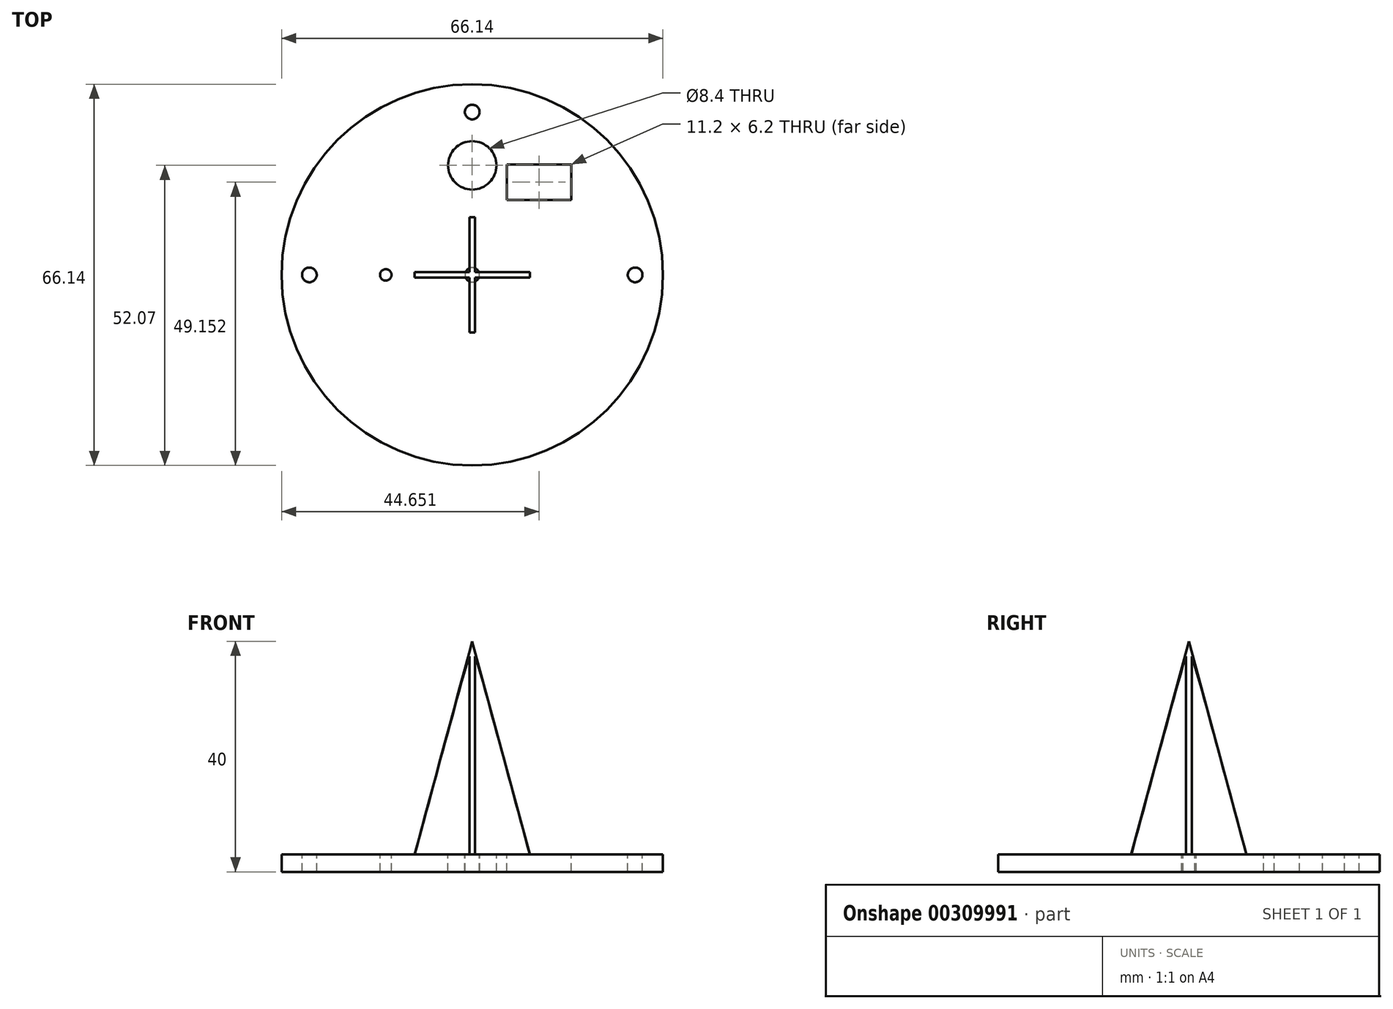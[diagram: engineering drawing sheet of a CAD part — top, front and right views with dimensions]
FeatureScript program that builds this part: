
annotation { "Feature Type Name" : "Feature", "Feature Type Description" : "" }
export const myFeature = defineFeature(function(context is Context, id is Id, definition is map)
    precondition{}
    {
        {
            var Q0;
            Q0=qCreatedBy(makeId("Top.planeOp"),FACE);
            var sketch = newSketch(context, id + "F0", { "sketchPlane" : qUnion([Q0])});
            skPoint(sketch, "E0.4", {"position": v(0, 0) * mm});
            skCircle(sketch, "E1", {"center": v(0, 0) * mm, "radius": 33.07 * mm});
            skPoint(sketch, "E2", {"position": v(-28.25, 0) * mm});
            skPoint(sketch, "E3", {"position": v(-15, 0) * mm});
            skPoint(sketch, "E4", {"position": v(0, 19) * mm});
            skPoint(sketch, "E5", {"position": v(0, 28.25) * mm});
            skCircle(sketch, "E6", {"center": v(0, 0) * mm, "radius": 1.25 * mm});
            skCircle(sketch, "E7", {"center": v(0, 19) * mm, "radius": 4.2 * mm});
            skLineSegment(sketch, "E8.bottom", {"start": v(5.98, 12.98) * mm, "end": v(17.18, 12.98) * mm});
            skLineSegment(sketch, "E8.top", {"start": v(5.98, 19.18) * mm, "end": v(17.18, 19.18) * mm});
            skLineSegment(sketch, "E8.left", {"start": v(5.98, 12.98) * mm, "end": v(5.98, 19.18) * mm});
            skLineSegment(sketch, "E8.right", {"start": v(17.18, 12.98) * mm, "end": v(17.18, 19.18) * mm});
            skPoint(sketch, "E9", {"position": v(17.18, 19.18) * mm});
            skPoint(sketch, "E10", {"position": v(5.98, 12.98) * mm});
            skLineSegment(sketch, "E11", {"start": v(21.45, 16.08) * mm, "end": v(-17.9, 16.08) * mm, "construction": true});
            skLineSegment(sketch, "E12", {"start": v(11.58, 19.58) * mm, "end": v(11.58, -2.2) * mm, "construction": true});
            skCircle(sketch, "E13", {"center": v(-15, 0) * mm, "radius": 1 * mm});
            skCircle(sketch, "E14", {"center": v(-28.25, 0) * mm, "radius": 1.02 * mm});
            skCircle(sketch, "E15", {"center": v(-28.25, 0) * mm, "radius": 1.28 * mm});
            skCircle(sketch, "E16.MirrorC", {"center": v(28.25, 0) * mm, "radius": 1.02 * mm});
            skCircle(sketch, "E17.MirrorC", {"center": v(28.25, 0) * mm, "radius": 1.28 * mm});
            skLineSegment(sketch, "E18.bottom", {"start": v(60, 80) * mm, "end": v(-20, 80) * mm});
            skLineSegment(sketch, "E18.top", {"start": v(60, -20) * mm, "end": v(-20, -20) * mm});
            skLineSegment(sketch, "E18.left", {"start": v(60, 80) * mm, "end": v(60, -20) * mm});
            skLineSegment(sketch, "E18.right", {"start": v(-20, 80) * mm, "end": v(-20, -20) * mm});
            skLineSegment(sketch, "E19.bottom", {"start": v(75, 95) * mm, "end": v(-35, 95) * mm});
            skLineSegment(sketch, "E19.top", {"start": v(75, -35) * mm, "end": v(-35, -35) * mm});
            skLineSegment(sketch, "E19.left", {"start": v(75, 95) * mm, "end": v(75, -35) * mm});
            skLineSegment(sketch, "E19.right", {"start": v(-35, 95) * mm, "end": v(-35, -35) * mm});
            skCircle(sketch, "E20", {"center": v(0, 28.25) * mm, "radius": 1.28 * mm});
            skCircle(sketch, "E21", {"center": v(0, 28.25) * mm, "radius": 1.02 * mm});
            skSolve(sketch);
        }
        {
            var Q0;
            Q0=makeQuery(id+"F0.imprint","IMPRINT",FACE,{"disambiguationData":[TD([[makeQuery(id+"F0.imprint","IMPRINT",EDGE,{"derivedFrom":sQuery(id+"F0.wireOp",EDGE,"E6")}),-1.0]])]});
            var Q1;
            Q1=makeQuery(id+"F0.imprint","IMPRINT",FACE,{"disambiguationData":[TD([[makeQuery(id+"F0.imprint","IMPRINT",EDGE,{"derivedFrom":sQuery(id+"F0.wireOp",EDGE,"E15")}),-1.0]])]});
            extrude(context, id + "F1", {"entities" : qUnion([Q0, Q1]), "oppositeDirection" : true, "depth" : 3 * mm});
        }
        {
            var Q0;
            Q0=qCreatedBy(makeId("Right.planeOp"),FACE);
            var sketch = newSketch(context, id + "F2", { "sketchPlane" : qUnion([Q0])});
            skLineSegment(sketch, "E22", {"start": v(0, 37) * mm, "end": v(0, 0) * mm});
            skLineSegment(sketch, "E23", {"start": v(0, 0) * mm, "end": v(10, 0) * mm});
            skLineSegment(sketch, "E24", {"start": v(10, 0) * mm, "end": v(0, 37) * mm});
            skSolve(sketch);
        }
        {
            var Q0;
            Q0=makeQuery(id+"F2.imprint","IMPRINT",FACE,{"disambiguationData":[TD([[makeQuery(id+"F2.imprint","IMPRINT",EDGE,{"derivedFrom":sQuery(id+"F2.wireOp",EDGE,"E22")}),1.0]])]});
            var Q1;
            Q1=sQuery(id+"F2.wireOp",EDGE,"E22");
            revolve(context, id + "F3", {"operationType" : NewBodyOperationType.ADD, "entities" : qUnion([Q0]), "axis" : qUnion([Q1]), "revolveType" : RevolveType.FULL});
        }
        {
            var Q0;
            Q0=qCreatedBy(makeId("Top.planeOp"),FACE);
            var sketch = newSketch(context, id + "F4", { "sketchPlane" : qUnion([Q0])});
            skLineSegment(sketch, "E25.bottom", {"start": v(-0.5, 11.34) * mm, "end": v(-11.34, 11.34) * mm});
            skLineSegment(sketch, "E25.top", {"start": v(-0.5, 0.5) * mm, "end": v(-11.34, 0.5) * mm});
            skLineSegment(sketch, "E25.left", {"start": v(-0.5, 11.34) * mm, "end": v(-0.5, 0.5) * mm});
            skLineSegment(sketch, "E25.right", {"start": v(-11.34, 11.34) * mm, "end": v(-11.34, 0.5) * mm});
            skLineSegment(sketch, "E26.MirrorCS", {"start": v(0.5, 11.34) * mm, "end": v(0.5, 0.5) * mm});
            skLineSegment(sketch, "E27.MirrorCS", {"start": v(0.5, 0.5) * mm, "end": v(11.34, 0.5) * mm});
            skLineSegment(sketch, "E28.MirrorCS", {"start": v(0.5, 11.34) * mm, "end": v(11.34, 11.34) * mm});
            skLineSegment(sketch, "E29.MirrorCS", {"start": v(11.34, 11.34) * mm, "end": v(11.34, 0.5) * mm});
            skLineSegment(sketch, "E30.MirrorCS", {"start": v(-0.5, -0.5) * mm, "end": v(-11.34, -0.5) * mm});
            skLineSegment(sketch, "E31.MirrorCS", {"start": v(-11.34, -11.34) * mm, "end": v(-11.34, -0.5) * mm});
            skLineSegment(sketch, "E32.MirrorCS", {"start": v(-0.5, -11.34) * mm, "end": v(-11.34, -11.34) * mm});
            skLineSegment(sketch, "E33.MirrorCS", {"start": v(0.5, -0.5) * mm, "end": v(11.34, -0.5) * mm});
            skLineSegment(sketch, "E34.MirrorCS", {"start": v(11.34, -11.34) * mm, "end": v(11.34, -0.5) * mm});
            skLineSegment(sketch, "E35.MirrorCS", {"start": v(0.5, -11.34) * mm, "end": v(11.34, -11.34) * mm});
            skLineSegment(sketch, "E36.MirrorCS", {"start": v(0.5, -11.34) * mm, "end": v(0.5, -0.5) * mm});
            skLineSegment(sketch, "E37.MirrorCS", {"start": v(-0.5, -11.34) * mm, "end": v(-0.5, -0.5) * mm});
            skSolve(sketch);
        }
        {
            var Q0;
            Q0=makeQuery(id+"F4.imprint","IMPRINT",FACE,{"disambiguationData":[TD([[makeQuery(id+"F4.imprint","IMPRINT",EDGE,{"derivedFrom":sQuery(id+"F4.wireOp",EDGE,"E25.bottom")}),1.0]])]});
            var Q1;
            Q1=makeQuery(id+"F4.imprint","IMPRINT",FACE,{"disambiguationData":[TD([[makeQuery(id+"F4.imprint","IMPRINT",EDGE,{"derivedFrom":sQuery(id+"F4.wireOp",EDGE,"E27.MirrorCS")}),1.0]])]});
            var Q2;
            Q2=makeQuery(id+"F4.imprint","IMPRINT",FACE,{"disambiguationData":[TD([[makeQuery(id+"F4.imprint","IMPRINT",EDGE,{"derivedFrom":sQuery(id+"F4.wireOp",EDGE,"E33.MirrorCS")}),-1.0]])]});
            var Q3;
            Q3=makeQuery(id+"F4.imprint","IMPRINT",FACE,{"disambiguationData":[TD([[makeQuery(id+"F4.imprint","IMPRINT",EDGE,{"derivedFrom":sQuery(id+"F4.wireOp",EDGE,"E30.MirrorCS")}),1.0]])]});
            extrude(context, id + "F5", {"entities" : qUnion([Q0, Q1, Q2, Q3]), "operationType" : NewBodyOperationType.REMOVE, "depth" : 40 * mm});
        }
    });
